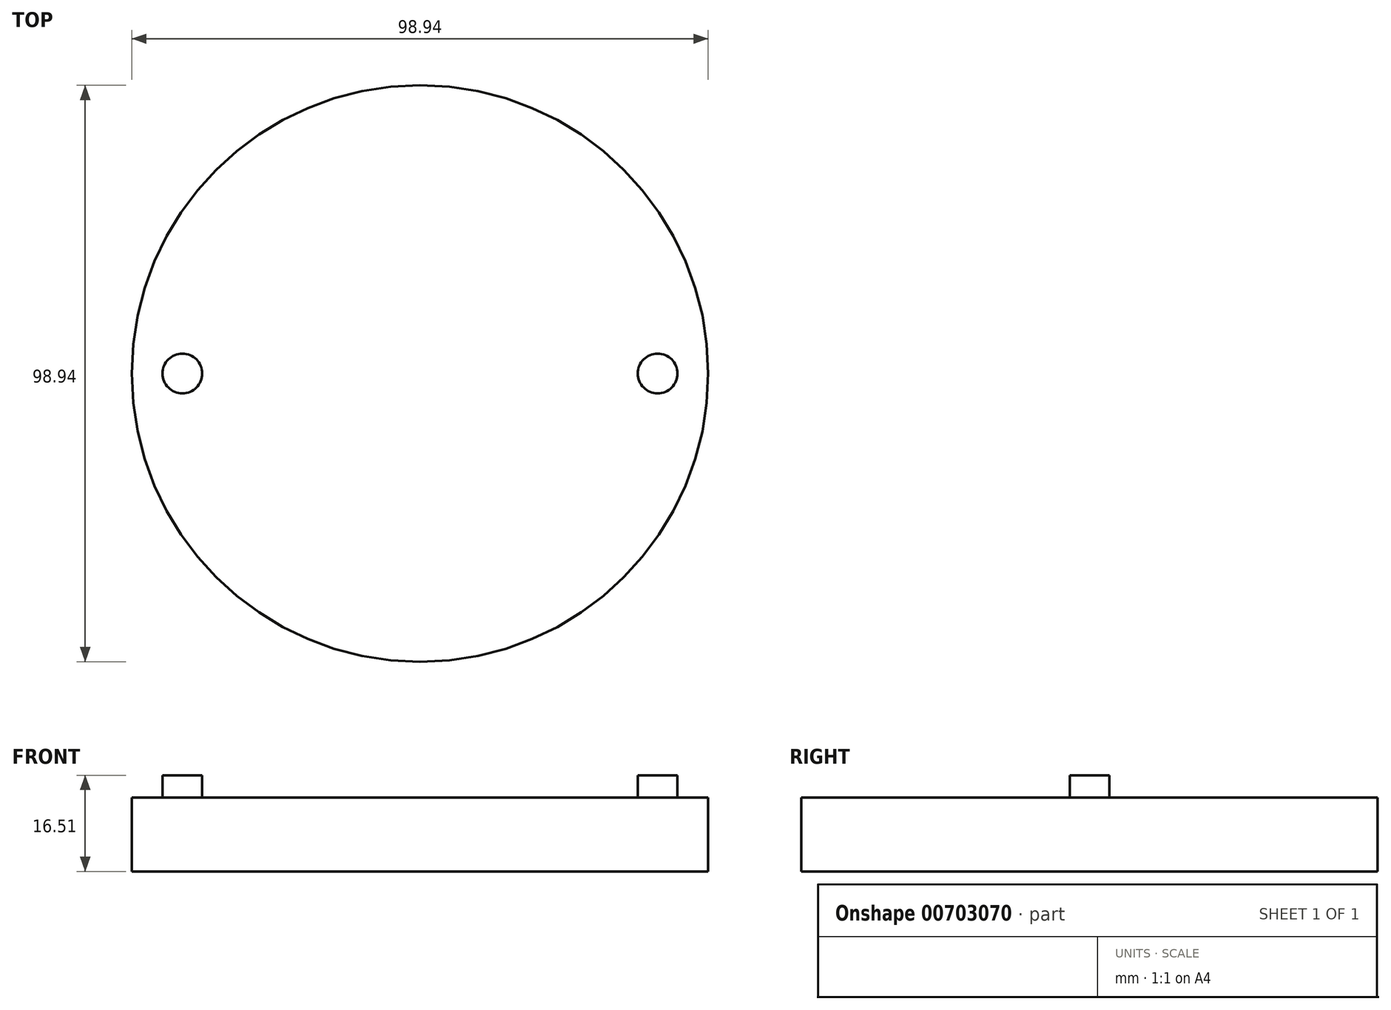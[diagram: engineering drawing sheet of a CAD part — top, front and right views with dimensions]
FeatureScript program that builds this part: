
annotation { "Feature Type Name" : "Feature", "Feature Type Description" : "" }
export const myFeature = defineFeature(function(context is Context, id is Id, definition is map)
    precondition{}
    {
        {
            var Q0;
            Q0=qCreatedBy(makeId("Top.planeOp"),FACE);
            var sketch = newSketch(context, id + "F0", { "sketchPlane" : qUnion([Q0])});
            skCircle(sketch, "E0", {"center": v(0, 0) * mm, "radius": 49.47 * mm});
            skSolve(sketch);
        }
        {
            var Q0;
            Q0 = qSketchRegion(id + "F0", true);
            extrude(context, id + "F1", {"entities" : qUnion([Q0]), "oppositeDirection" : true, "depth" : 12.7 * mm, "offsetDistance" : 25.4 * mm});
        }
        {
            var Q0;
            Q0=qCreatedBy(makeId("Top.planeOp"),FACE);
            var sketch = newSketch(context, id + "F2", { "sketchPlane" : qUnion([Q0])});
            skLineSegment(sketch, "E1", {"start": v(0, 57.63) * mm, "end": v(0, -63.98) * mm});
            skCircle(sketch, "E2", {"center": v(40.8, 0) * mm, "radius": 3.4 * mm});
            skCircle(sketch, "E3.MirrorC", {"center": v(-40.8, 0) * mm, "radius": 3.4 * mm});
            skSolve(sketch);
        }
        {
            var Q0;
            Q0 = qSketchRegion(id + "F2", true);
            extrude(context, id + "F3", {"entities" : qUnion([Q0]), "depth" : 3.8 * mm, "offsetDistance" : 25.4 * mm});
        }
    });
